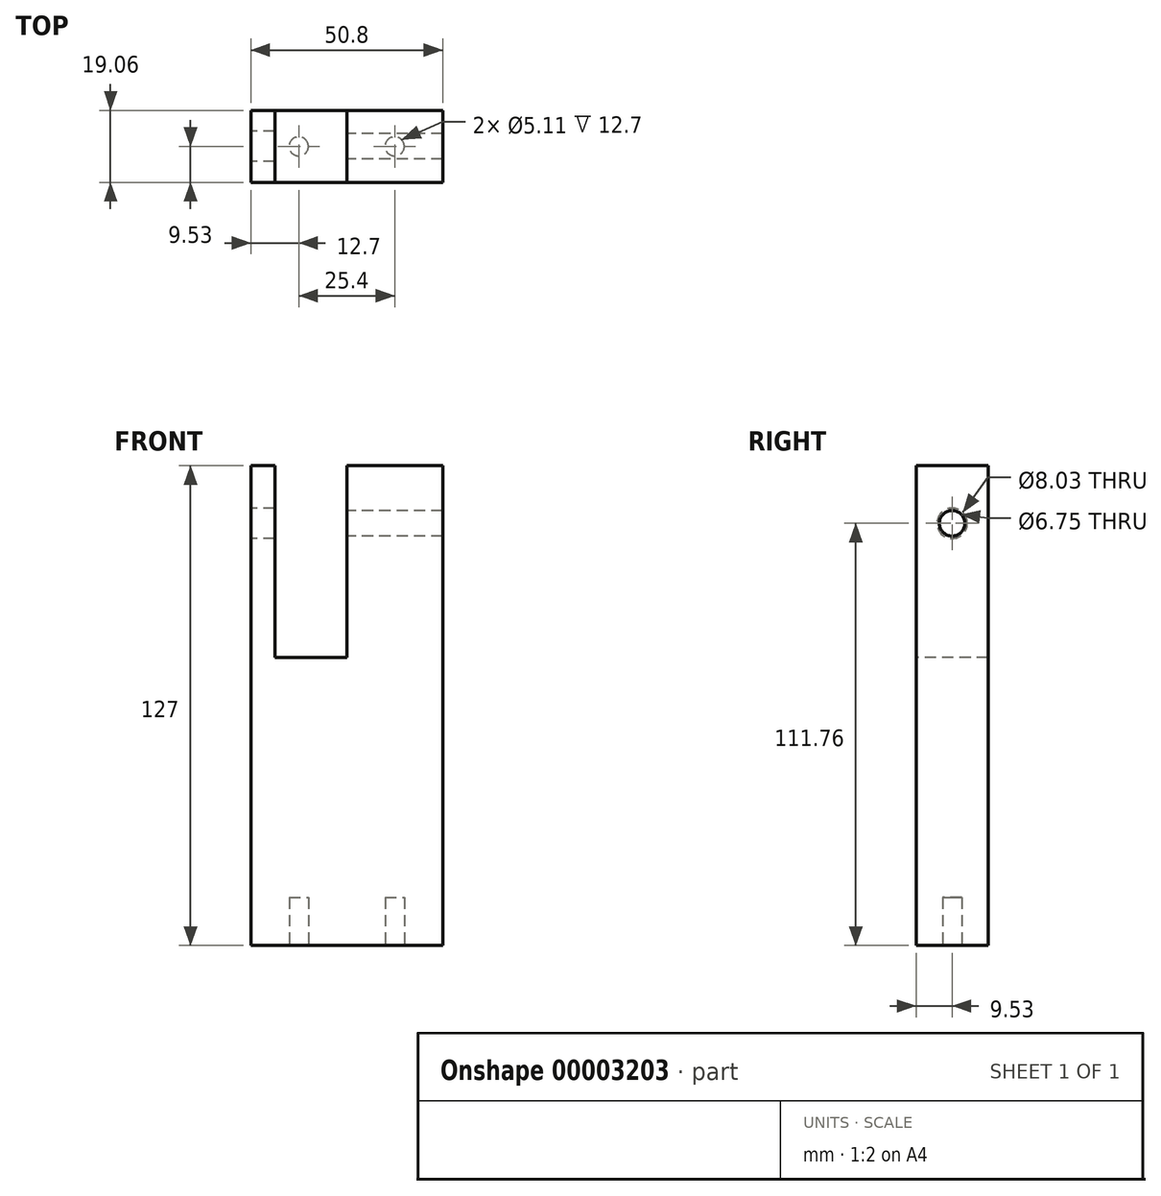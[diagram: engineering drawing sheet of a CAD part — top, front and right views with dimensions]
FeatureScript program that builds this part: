
annotation { "Feature Type Name" : "Feature", "Feature Type Description" : "" }
export const myFeature = defineFeature(function(context is Context, id is Id, definition is map)
    precondition{}
    {
        {
            var Q0;
            Q0=qCreatedBy(makeId("Front.planeOp"),FACE);
            var sketch = newSketch(context, id + "F0", { "sketchPlane" : qUnion([Q0])});
            skLineSegment(sketch, "E0", {"start": v(0, 0) * mm, "end": v(0, -127) * mm});
            skLineSegment(sketch, "E1", {"start": v(0, -127) * mm, "end": v(50.8, -127) * mm});
            skLineSegment(sketch, "E2", {"start": v(50.8, -127) * mm, "end": v(50.8, 0) * mm});
            skLineSegment(sketch, "E3", {"start": v(50.8, 0) * mm, "end": v(0, 0) * mm});
            skSolve(sketch);
        }
        {
            var Q0;
            Q0=makeQuery(id+"F0.imprint","IMPRINT",FACE,{"disambiguationData":[TD([[makeQuery(id+"F0.imprint","IMPRINT",EDGE,{"derivedFrom":sQuery(id+"F0.wireOp",EDGE,"E0")}),1.0]])]});
            extrude(context, id + "F1", {"entities" : qUnion([Q0]), "endBound" : BoundingType.SYMMETRIC, "depth" : 19.05 * mm});
        }
        {
            var Q0;
            Q0=makeQuery(id+"F1.opExtrude","CAP_FACE",FACE,{"disambiguationData":[OSD([sQuery(id+"F0.wireOp",EDGE,"E0"),sQuery(id+"F0.wireOp",EDGE,"E1"),sQuery(id+"F0.wireOp",EDGE,"E2"),sQuery(id+"F0.wireOp",EDGE,"E3")])],"isStart":false});
            var sketch = newSketch(context, id + "F2", { "sketchPlane" : qUnion([Q0])});
            skLineSegment(sketch, "E4", {"start": v(6.35, 0) * mm, "end": v(6.35, -50.8) * mm});
            skLineSegment(sketch, "E5", {"start": v(6.35, -50.8) * mm, "end": v(25.4, -50.8) * mm});
            skLineSegment(sketch, "E6", {"start": v(25.4, -50.8) * mm, "end": v(25.4, 0) * mm});
            skLineSegment(sketch, "E7", {"start": v(6.35, 0) * mm, "end": v(25.4, 0) * mm});
            skSolve(sketch);
        }
        {
            var Q0;
            Q0 = qSketchRegion(id + "F2", true);
            extrude(context, id + "F3", {"entities" : qUnion([Q0]), "operationType" : NewBodyOperationType.REMOVE, "endBound" : BoundingType.THROUGH_ALL, "oppositeDirection" : true, "depth" : 25.4 * mm});
        }
        {
            var Q0;
            Q0=makeQuery(id+"F1.opExtrude","SWEPT_FACE",FACE,{"disambiguationData":[OSD([sQuery(id+"F0.wireOp",EDGE,"E0")])]});
            var sketch = newSketch(context, id + "F4", { "sketchPlane" : qUnion([Q0])});
            skCircle(sketch, "E8", {"center": v(0, -15.24) * mm, "radius": 4.01 * mm});
            skSolve(sketch);
        }
        {
            var Q0;
            Q0 = qSketchRegion(id + "F4", true);
            extrude(context, id + "F5", {"entities" : qUnion([Q0]), "operationType" : NewBodyOperationType.REMOVE, "oppositeDirection" : true, "depth" : 7.62 * mm});
        }
        {
            var Q0;
            Q0=makeQuery(id+"F3.boolean.opBoolean","COPY",FACE,{"derivedFrom":makeQuery(id+"F3.opExtrude","SWEPT_FACE",FACE,{"disambiguationData":[OSD([sQuery(id+"F2.wireOp",EDGE,"E6")])]})});
            var sketch = newSketch(context, id + "F6", { "sketchPlane" : qUnion([Q0])});
            skLineSegment(sketch, "E9", {"start": v(0, 0) * mm, "end": v(0, -27.9) * mm, "construction": true});
            skLineSegment(sketch, "E10", {"start": v(-9.53, -15.24) * mm, "end": v(9.53, -15.24) * mm, "construction": true});
            skCircle(sketch, "E11", {"center": v(0, -15.24) * mm, "radius": 3.37 * mm});
            skSolve(sketch);
        }
        {
            var Q0;
            Q0=makeQuery(id+"F6.imprint","IMPRINT",FACE,{"disambiguationData":[TD([[makeQuery(id+"F6.imprint","IMPRINT",EDGE,{"derivedFrom":sQuery(id+"F6.wireOp",EDGE,"E11")}),1.0]])]});
            extrude(context, id + "F7", {"entities" : qUnion([Q0]), "operationType" : NewBodyOperationType.REMOVE, "endBound" : BoundingType.THROUGH_ALL, "oppositeDirection" : true, "depth" : 25.4 * mm});
        }
        {
            var Q0;
            Q0=makeQuery(id+"F1.opExtrude","SWEPT_FACE",FACE,{"disambiguationData":[OSD([sQuery(id+"F0.wireOp",EDGE,"E1")])]});
            var sketch = newSketch(context, id + "F8", { "sketchPlane" : qUnion([Q0])});
            skCircle(sketch, "E12", {"center": v(12.7, 0) * mm, "radius": 2.55 * mm});
            skCircle(sketch, "E13", {"center": v(38.1, 0) * mm, "radius": 2.55 * mm});
            skSolve(sketch);
        }
        {
            var Q0;
            Q0=makeQuery(id+"F8.imprint","IMPRINT",FACE,{"disambiguationData":[TD([[makeQuery(id+"F8.imprint","IMPRINT",EDGE,{"derivedFrom":sQuery(id+"F8.wireOp",EDGE,"E13")}),1.0]])]});
            var Q1;
            Q1=makeQuery(id+"F8.imprint","IMPRINT",FACE,{"disambiguationData":[TD([[makeQuery(id+"F8.imprint","IMPRINT",EDGE,{"derivedFrom":sQuery(id+"F8.wireOp",EDGE,"E12")}),1.0]])]});
            extrude(context, id + "F9", {"entities" : qUnion([Q0, Q1]), "operationType" : NewBodyOperationType.REMOVE, "oppositeDirection" : true, "depth" : 12.7 * mm});
        }
    });
